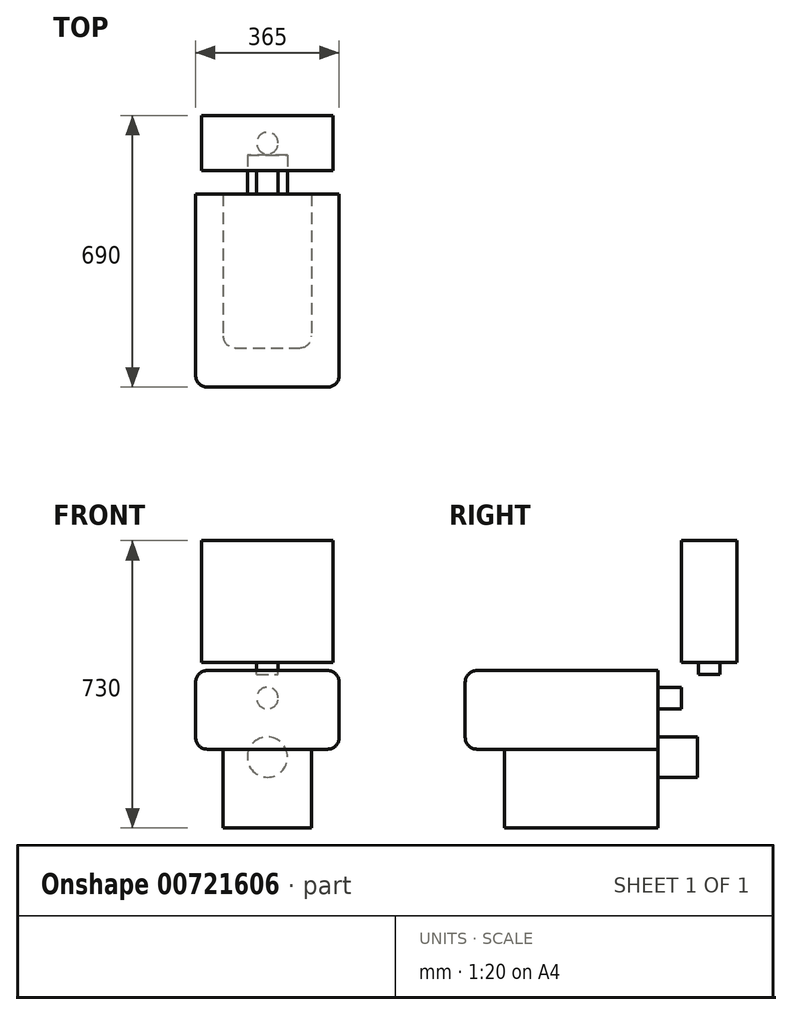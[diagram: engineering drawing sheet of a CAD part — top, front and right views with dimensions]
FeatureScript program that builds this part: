
annotation { "Feature Type Name" : "Feature", "Feature Type Description" : "" }
export const myFeature = defineFeature(function(context is Context, id is Id, definition is map)
    precondition{}
    {
        {
            var Q0;
            Q0=qCreatedBy(makeId("Top.planeOp"),FACE);
            var sketch = newSketch(context, id + "F0", { "sketchPlane" : qUnion([Q0])});
            skLineSegment(sketch, "E0.bottom", {"start": v(0, 0) * mm, "end": v(225, 0) * mm});
            skLineSegment(sketch, "E0.top", {"start": v(0, -390) * mm, "end": v(225, -390) * mm});
            skLineSegment(sketch, "E0.left", {"start": v(0, 0) * mm, "end": v(0, -390) * mm});
            skLineSegment(sketch, "E0.right", {"start": v(225, 0) * mm, "end": v(225, -390) * mm});
            skSolve(sketch);
        }
        {
            var Q0;
            Q0=makeQuery(id+"F0.imprint","IMPRINT",FACE,{"disambiguationData":[TD([[makeQuery(id+"F0.imprint","IMPRINT",EDGE,{"derivedFrom":sQuery(id+"F0.wireOp",EDGE,"E0.bottom")}),-1.0]])]});
            extrude(context, id + "F1", {"entities" : qUnion([Q0]), "depth" : 200 * mm, "offsetDistance" : 25 * mm});
        }
        {
            var Q0;
            Q0=makeQuery(id+"F1.opExtrude","CAP_FACE",FACE,{"disambiguationData":[OSD([sQuery(id+"F0.wireOp",EDGE,"E0.bottom"),sQuery(id+"F0.wireOp",EDGE,"E0.top"),sQuery(id+"F0.wireOp",EDGE,"E0.left"),sQuery(id+"F0.wireOp",EDGE,"E0.right")])],"isStart":false});
            var sketch = newSketch(context, id + "F2", { "sketchPlane" : qUnion([Q0])});
            skLineSegment(sketch, "E1", {"start": v(112.5, -195) * mm, "end": v(-70, -195) * mm});
            skPoint(sketch, "E1.startSnap0", {"position": v(112.5, -390) * mm});
            skPoint(sketch, "E1.startSnap1", {"position": v(0, -195) * mm});
            skLineSegment(sketch, "E2", {"start": v(112.5, 0) * mm, "end": v(112.5, -490) * mm});
            skLineSegment(sketch, "E3.bottom", {"start": v(-70, -490) * mm, "end": v(295, -490) * mm});
            skLineSegment(sketch, "E3.top", {"start": v(-70, 0) * mm, "end": v(295, 0) * mm});
            skLineSegment(sketch, "E3.left", {"start": v(-70, -490) * mm, "end": v(-70, 0) * mm});
            skLineSegment(sketch, "E3.right", {"start": v(295, -490) * mm, "end": v(295, 0) * mm});
            skSolve(sketch);
        }
        {
            var Q0;
            Q0 = qSketchRegion(id + "F2", true);
            extrude(context, id + "F3", {"entities" : qUnion([Q0]), "operationType" : NewBodyOperationType.ADD, "depth" : 200 * mm, "offsetDistance" : 25 * mm});
        }
        {
            var Q0;
            Q0=makeQuery(id+"F1.opExtrude","SWEPT_EDGE",EDGE,{"disambiguationData":[OSD([sQuery(id+"F0.wireOp",EDGE,"E0.top"),sQuery(id+"F0.wireOp",EDGE,"E0.right")])]});
            var Q1;
            Q1=makeQuery(id+"F1.opExtrude","CAP_EDGE",EDGE,{"disambiguationData":[OSD([sQuery(id+"F0.wireOp",EDGE,"E0.top")])],"isStart":false});
            var Q2;
            Q2=makeQuery(id+"F1.opExtrude","SWEPT_EDGE",EDGE,{"disambiguationData":[OSD([sQuery(id+"F0.wireOp",EDGE,"E0.top"),sQuery(id+"F0.wireOp",EDGE,"E0.left")])]});
            var Q3;
            Q3=makeQuery(id+"F3.opExtrude","CAP_EDGE",EDGE,{"disambiguationData":[OSD([sQuery(id+"F2.wireOp",EDGE,"E3.right")])],"isStart":true});
            var Q4;
            Q4=makeQuery(id+"F3.opExtrude","CAP_EDGE",EDGE,{"disambiguationData":[OSD([sQuery(id+"F2.wireOp",EDGE,"E3.bottom")])],"isStart":true});
            var Q5;
            Q5=makeQuery(id+"F3.opExtrude","CAP_EDGE",EDGE,{"disambiguationData":[OSD([sQuery(id+"F2.wireOp",EDGE,"E3.left")])],"isStart":true});
            var Q6;
            Q6=makeQuery(id+"F3.opExtrude","SWEPT_EDGE",EDGE,{"disambiguationData":[OSD([sQuery(id+"F2.wireOp",EDGE,"E3.bottom"),sQuery(id+"F2.wireOp",EDGE,"E3.left")])]});
            var Q7;
            Q7=makeQuery(id+"F3.opExtrude","SWEPT_EDGE",EDGE,{"disambiguationData":[OSD([sQuery(id+"F2.wireOp",EDGE,"E3.bottom"),sQuery(id+"F2.wireOp",EDGE,"E3.right")])]});
            var Q8;
            Q8=makeQuery(id+"F3.opExtrude","CAP_EDGE",EDGE,{"disambiguationData":[OSD([sQuery(id+"F2.wireOp",EDGE,"E3.bottom")])],"isStart":false});
            var Q9;
            Q9=makeQuery(id+"F3.opExtrude","CAP_EDGE",EDGE,{"disambiguationData":[OSD([sQuery(id+"F2.wireOp",EDGE,"E3.left")])],"isStart":false});
            var Q10;
            Q10=makeQuery(id+"F3.opExtrude","CAP_EDGE",EDGE,{"disambiguationData":[OSD([sQuery(id+"F2.wireOp",EDGE,"E3.right")])],"isStart":false});
            fillet(context, id + "F4", {"entities" : qUnion([Q0, Q1, Q2, Q3, Q4, Q5, Q6, Q7, Q8, Q9, Q10]), "radius" : 30 * mm, "tangentPropagation" : true, "allowEdgeOverflow" : false});
        }
        {
            var Q0;
            Q0=makeQuery(id+"F3.boolean.opBoolean","MERGE",FACE,{"derivedFrom":[makeQuery(id+"F1.opExtrude","SWEPT_FACE",FACE,{"disambiguationData":[OSD([sQuery(id+"F0.wireOp",EDGE,"E0.bottom")])]}),makeQuery(id+"F3.opExtrude","SWEPT_FACE",FACE,{"disambiguationData":[OSD([sQuery(id+"F2.wireOp",EDGE,"E3.top")])]})]});
            var sketch = newSketch(context, id + "F5", { "sketchPlane" : qUnion([Q0])});
            skCircle(sketch, "E4", {"center": v(-112.5, 330) * mm, "radius": 27.5 * mm});
            skPoint(sketch, "E4.centerSnap0", {"position": v(-112.5, 0) * mm});
            skCircle(sketch, "E5", {"center": v(-112.5, 180) * mm, "radius": 51 * mm});
            skSolve(sketch);
        }
        {
            var Q0;
            Q0=makeQuery(id+"F5.imprint","IMPRINT",FACE,{"disambiguationData":[TD([[makeQuery(id+"F5.imprint","IMPRINT",EDGE,{"derivedFrom":sQuery(id+"F5.wireOp",EDGE,"E5")}),1.0]])]});
            extrude(context, id + "F6", {"entities" : qUnion([Q0]), "operationType" : NewBodyOperationType.ADD, "depth" : 100 * mm, "offsetDistance" : 25 * mm});
        }
        {
            var Q0;
            Q0=makeQuery(id+"F5.imprint","IMPRINT",FACE,{"disambiguationData":[TD([[makeQuery(id+"F5.imprint","IMPRINT",EDGE,{"derivedFrom":sQuery(id+"F5.wireOp",EDGE,"E4")}),1.0]])]});
            extrude(context, id + "F7", {"entities" : qUnion([Q0]), "operationType" : NewBodyOperationType.ADD, "depth" : 60 * mm, "offsetDistance" : 25 * mm});
        }
        {
            var Q0;
            Q0=makeQuery(id+"F3.opExtrude","CAP_FACE",FACE,{"disambiguationData":[OSD([sQuery(id+"F2.wireOp",EDGE,"E3.bottom"),sQuery(id+"F2.wireOp",EDGE,"E3.top"),sQuery(id+"F2.wireOp",EDGE,"E3.left"),sQuery(id+"F2.wireOp",EDGE,"E3.right")])],"isStart":false});
            cPlane(context, id + "F8", {"entities" : qUnion([Q0]), "cplaneType" : CPlaneType.OFFSET, "offset" : 20 * mm, "width" : 150 * mm, "height" : 150 * mm});
        }
        {
            var Q0;
            Q0=qCreatedBy(id+"F8.planeOp",FACE);
            var sketch = newSketch(context, id + "F9", { "sketchPlane" : qUnion([Q0])});
            skLineSegment(sketch, "E6", {"start": v(112.5, 60) * mm, "end": v(279.5, 60) * mm});
            skLineSegment(sketch, "E7.bottom", {"start": v(279.5, 60) * mm, "end": v(-54.5, 60) * mm});
            skLineSegment(sketch, "E7.top", {"start": v(279.5, 200) * mm, "end": v(-54.5, 200) * mm});
            skLineSegment(sketch, "E7.left", {"start": v(279.5, 60) * mm, "end": v(279.5, 200) * mm});
            skLineSegment(sketch, "E7.right", {"start": v(-54.5, 60) * mm, "end": v(-54.5, 200) * mm});
            skSolve(sketch);
        }
        {
            var Q0;
            Q0=makeQuery(id+"F9.imprint","IMPRINT",FACE,{"disambiguationData":[TD([[makeQuery(id+"F9.imprint","IMPRINT",EDGE,{"derivedFrom":sQuery(id+"F9.wireOp",EDGE,"E7.top")}),1.0]])]});
            extrude(context, id + "F10", {"entities" : qUnion([Q0]), "depth" : 310 * mm, "offsetDistance" : 25 * mm});
        }
        {
            var Q0;
            Q0=makeQuery(id+"F10.opExtrude","CAP_FACE",FACE,{"disambiguationData":[OSD([sQuery(id+"F9.wireOp",EDGE,"E7.bottom"),sQuery(id+"F9.wireOp",EDGE,"E7.top"),sQuery(id+"F9.wireOp",EDGE,"E7.left"),sQuery(id+"F9.wireOp",EDGE,"E7.right")])],"isStart":true});
            var sketch = newSketch(context, id + "F11", { "sketchPlane" : qUnion([Q0])});
            skCircle(sketch, "E8", {"center": v(112.5, -130) * mm, "radius": 27.5 * mm});
            skPoint(sketch, "E8.centerSnap0", {"position": v(112.5, -200) * mm});
            skPoint(sketch, "E8.centerSnap1", {"position": v(-54.5, -130) * mm});
            skSolve(sketch);
        }
        {
            var Q0;
            Q0=makeQuery(id+"F11.imprint","IMPRINT",FACE,{"disambiguationData":[TD([[makeQuery(id+"F11.imprint","IMPRINT",EDGE,{"derivedFrom":sQuery(id+"F11.wireOp",EDGE,"E8")}),1.0]])]});
            extrude(context, id + "F12", {"entities" : qUnion([Q0]), "operationType" : NewBodyOperationType.ADD, "depth" : 30 * mm, "offsetDistance" : 25 * mm});
        }
    });
